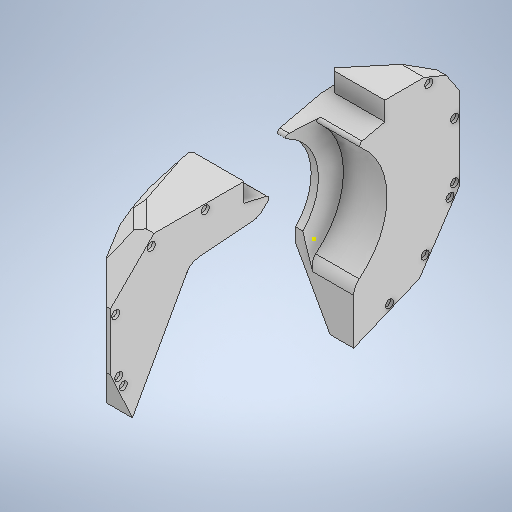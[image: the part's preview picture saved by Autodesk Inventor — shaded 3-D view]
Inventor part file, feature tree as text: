
AUTODESK INVENTOR PART (.ipt)
format: ipt  version: 2025.2 (Build 292293000, 293)  size: 737,280 bytes
history: native  units: mm
features: chamfer x21, reference x21, sketch x19, extrude x14, projected_geometry x6, fillet x5, other x4
ambient origin geometry x8: Origin, YZ Plane, XZ Plane, XY Plane, X Axis, Y Axis, Z Axis, Center Point
bodies: Solid1 (feature_tree), Solid2 (feature_tree)
feature tree (90):
  extrude  "Extrusion1"  Depth=76.5mm
  extrude  "Extrusion2"  Depth=4.0mm
  chamfer  "Chamfer1"  Distance=40.0mm Angle=360.0deg
  fillet  "Fillet1"  Radius=7.15585mm
  extrude  "Extrusion3"  Depth=40.0mm TaperAngle=360.0deg
  extrude  "Extrusion4"  Depth=40.0mm TaperAngle=360.0deg
  extrude  "Extrusion5"  Depth=28.0mm
  extrude  "Extrusion6"  Depth=35.5mm TaperAngle=0.0deg
  extrude  "Extrusion7"  Depth=3.0mm TaperAngle=45.0deg
  extrude  "Extrusion8"  Depth=3.0mm
  extrude  "Extrusion9"  TaperAngle=0.0deg  [1 undecoded]
  sketch  "Sketch15"  dims[d57=6.0mm d58=1.5mm d59=0.0mm d60=0.0mm d61=4.45mm]
  chamfer  "Chamfer2"  Distance=40.0mm Angle=360.0deg
  chamfer  "Chamfer3"  [1 undecoded]
  chamfer  "Chamfer4"  Distance=20.5mm
  extrude  "Extrusion11"  Depth=3.0mm
  extrude  "Extrusion12"  Depth=1.5mm
  chamfer  "Chamfer5"  [1 undecoded]
  fillet  "Fillet5"  Radius=4.45mm
  extrude  "Extrusion13"  Depth=22.0mm
  extrude  "Extrusion18"  Depth=6.0mm
  chamfer  "Chamfer27"  Distance=50.0mm
  chamfer  "Chamfer28"  Distance=30.0mm
  fillet  "Fillet7"  Radius=117.0mm
  chamfer  "Chamfer29"  Angle=45.0deg  [1 undecoded]
  chamfer  "Chamfer30"  Distance=92.0mm
  chamfer  "Chamfer31"  Distance=45.0mm
  chamfer  "Chamfer32"  Distance=52.0mm
  chamfer  "Chamfer33"  Distance=10.0mm
  chamfer  "Chamfer34"  Distance=2.5mm
  chamfer  "Chamfer35"  Distance=10.0mm
  chamfer  "Chamfer36"  Distance=2.0mm Angle=45.0deg
  chamfer  "Chamfer37"  Distance=20.0mm Angle=45.0deg
  chamfer  "Chamfer38"  Distance=10.0mm Angle=45.0deg
  chamfer  "Chamfer39"  Distance=35.0mm
  chamfer  "Chamfer40"  Distance=92.0mm
  chamfer  "Chamfer41"  Distance=2.5mm
  chamfer  "Chamfer42"  Distance=3.3mm
  fillet  "Fillet8"  [1 undecoded]
  fillet  "Fillet9"  Radius=3.0mm
  extrude  "Extrusion19"  Depth=4.0mm
  sketch  "Sketch1"  dims[d0=7.15585mm d1=76.5mm]
  sketch  "Sketch Circular Pattern2"  dims[d2=40.0mm d3=4.0mm]
  sketch  "Sketch Circular Pattern3"  dims[d18=7.1mm d19=40.0mm d21=360.0deg]
  sketch  "Sketch Circular Pattern4"  dims[d28=10.85mm d29=28.0mm]
  sketch  "Sketch2"  dims[d8=45.0deg d9=40.0mm d11=360.0deg d14=7.15585mm]
  sketch  "Sketch3"  dims[d23=21.7mm d24=40.0mm d26=360.0deg]
  sketch  "Sketch4"  dims[d31=6.6mm d32=0.0mm d33=35.5mm d34=0.0mm]
  sketch  "Sketch5"  dims[d35=43.0mm d36=3.0mm d37=35.5mm d38=45.0deg]
  sketch  "Sketch Circular Pattern5"  dims[d39=3.0mm d40=40.1mm]
  sketch  "Sketch6"  dims[d41=28.0mm d42=0.0mm d43=0.0mm d44=0.0mm]
  projected_geometry  "Projected Loop1"
  projected_geometry  "Projected Loop2"
  projected_geometry  "Projected Loop3"
  projected_geometry  "Projected Loop4"
  sketch  "Sketch7"  dims[d45=4.0mm d46=40.0mm d48=360.0deg d50=0.0mm d51=0.0mm]
  sketch  "Sketch8"  dims[d52=30.9mm d53=20.5mm d54=0.0mm]
  sketch  "Sketch13"  dims[d55=18.0mm d56=3.0mm]
  sketch  "Sketch16"  dims[d62=30.0mm d63=22.0mm]
  projected_geometry  "Projected Loop5"
  sketch  "Sketch18"  dims[d64=6.0mm d65=0.0mm d66=180.0mm]
  reference  "Reference3"
  reference  "Reference4"
  reference  "Reference5"
  reference  "Reference6"
  reference  "Reference7"
  reference  "Reference8"
  reference  "Reference9"
  reference  "Reference10"
  reference  "Reference11"
  reference  "Reference12"
  reference  "Reference13"
  reference  "Reference14"
  reference  "Reference15"
  reference  "Reference16"
  reference  "Reference18"
  reference  "Reference19"
  reference  "Reference20"
  reference  "Reference21"
  reference  "Reference22"
  reference  "Reference23"
  reference  "Reference24"
  sketch  "Sketch19"  dims[d67=90.0mm]
  projected_geometry  "Projected Loop6"
  sketch  "Sketch25"  dims[d68=92.0mm]
  sketch  "Sketch26"  dims[d85=100.0mm d86=50.0mm d87=30.0mm d88=117.0mm d89=45.0deg d90=92.0mm d91=45.0mm d92=52.0mm d93=10.0mm d94=2.5mm d95=10.0mm d96=0.0mm d104=30.0mm d105=2.0mm d106=45.0deg d107=20.0mm d108=2.0mm d109=45.0deg d110=10.0mm d111=2.0mm d112=45.0deg d113=35.0mm d114=0.0mm d115=92.0mm d116=2.5mm d117=3.3mm d118=0.0mm d119=0.0mm d120=3.0mm d121=35.0mm d122=45.0deg d123=4.0mm d124=100.0mm d125=4.0mm d130=40.0mm d131=0.0mm d192=10.0mm d205=51.0mm d206=5.0mm d207=0.0mm d208=5.0mm d209=12.25mm d210=45.0deg d212=5.0mm d213=12.25mm d214=45.0deg d215=2.0mm d216=33.5mm d217=12.25mm d218=45.0deg d219=37.0mm d220=12.25mm d221=45.0deg d222=12.25mm d223=12.25mm d224=45.0deg d225=12.25mm d226=12.25mm d227=45.0deg d228=12.25mm d229=12.25mm d230=45.0deg d231=12.25mm d232=12.25mm d233=45.0deg d234=12.25mm d235=12.25mm d236=45.0deg d237=37.0mm d238=12.25mm d239=45.0deg d240=16.0mm d241=12.25mm d242=45.0deg d243=16.0mm d244=12.25mm d245=45.0deg d246=16.0mm d247=12.25mm d248=45.0deg d249=16.0mm d250=12.25mm d251=45.0deg d252=3.5mm d253=12.25mm d254=45.0deg d255=3.5mm d256=12.25mm d257=45.0deg d258=2.0mm d259=10.0mm d260=5.6mm d261=5.6mm d262=5.6mm d263=5.6mm d264=5.6mm d265=5.6mm d266=5.6mm d267=5.6mm d268=5.6mm d269=5.6mm d270=5.6mm d271=2.0mm d272=0.0mm d193=0.5mm d194=0.872665mm d195=0.5mm d196=0.872665mm]
  parser-record x1  (decoder bookkeeping rows leaked as tree rows — omitted from the tree; the rows remain in map.json)
  other  "WBR.iam"
  other  "inner_body_c:1"
  other  "inner_body_b:1"
note: 5 required parameter values undecoded (feature->parameter linkage not recoverable at this tier; creation-order binding heuristic only, values carry confidence <= 0.55)
note: 1 file-system path scrubbed to <path> (originals preserved in map.json)
